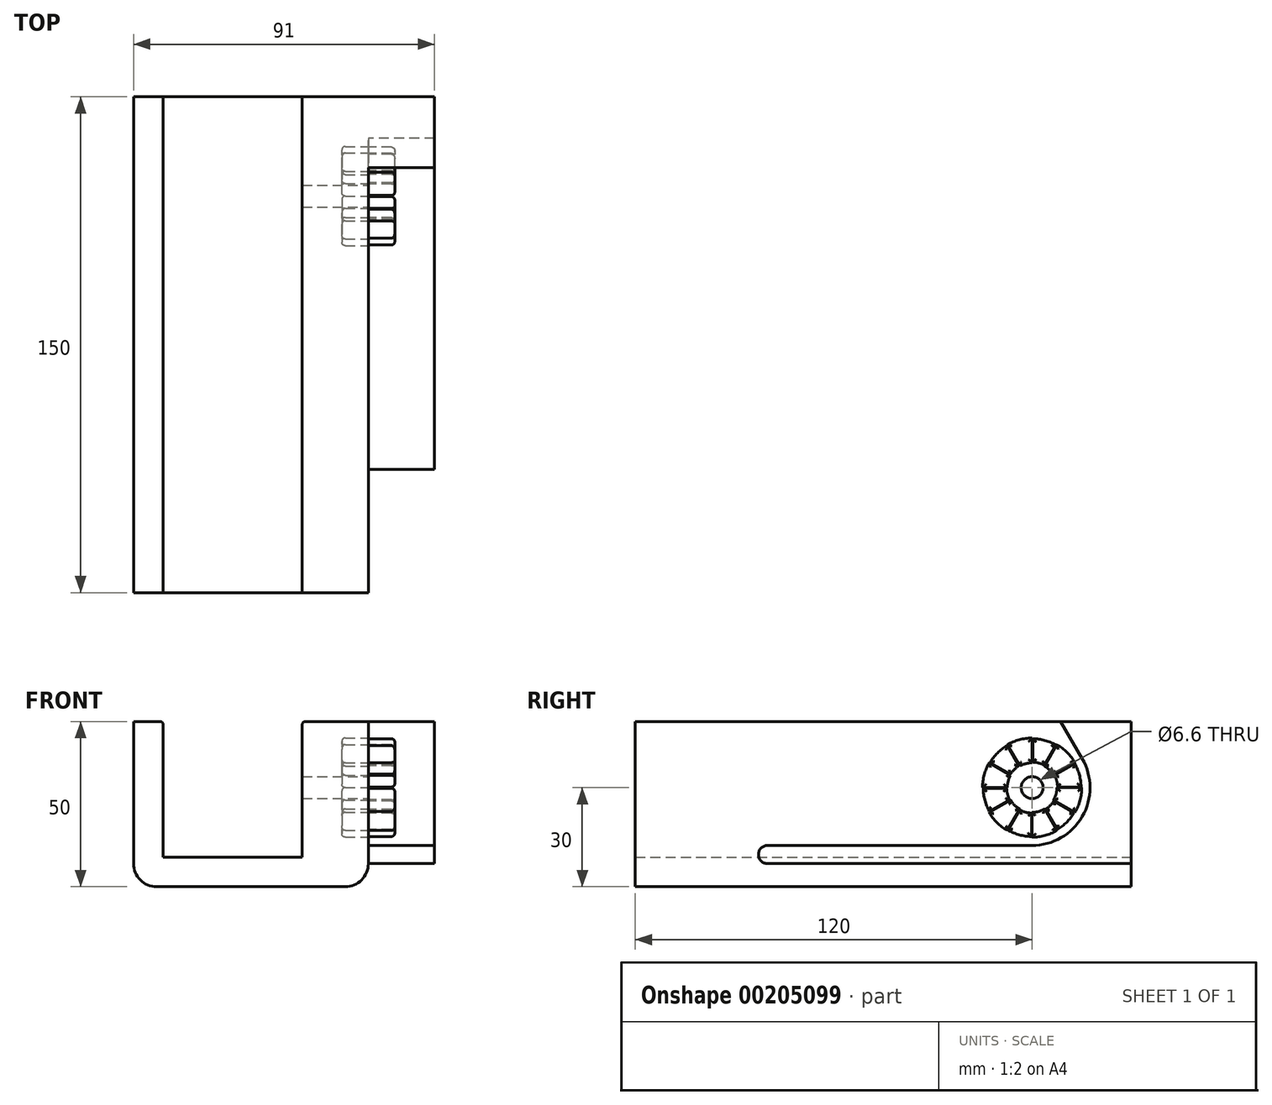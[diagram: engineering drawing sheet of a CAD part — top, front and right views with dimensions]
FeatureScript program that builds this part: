
annotation { "Feature Type Name" : "Feature", "Feature Type Description" : "" }
export const myFeature = defineFeature(function(context is Context, id is Id, definition is map)
    precondition{}
    {
        {
            var Q0;
            Q0=qCreatedBy(makeId("Front.planeOp"),FACE);
            var sketch = newSketch(context, id + "F7", { "sketchPlane" : qUnion([Q0])});
            skLineSegment(sketch, "E0", {"start": v(21, 0) * mm, "end": v(21, 40) * mm});
            skLineSegment(sketch, "E1", {"start": v(21, 0) * mm, "end": v(-21, 0) * mm});
            skLineSegment(sketch, "E2", {"start": v(-21, 0) * mm, "end": v(-21, 40) * mm});
            skLineSegment(sketch, "E3", {"start": v(-22, 41) * mm, "end": v(-30, 41) * mm});
            skLineSegment(sketch, "E4", {"start": v(-30, 41) * mm, "end": v(-30, -2) * mm});
            skLineSegment(sketch, "E5", {"start": v(-23, -9) * mm, "end": v(34, -9) * mm});
            skLineSegment(sketch, "E6", {"start": v(41, -2) * mm, "end": v(41, 41) * mm});
            skLineSegment(sketch, "E7", {"start": v(41, 41) * mm, "end": v(22, 41) * mm});
            skArc(sketch, "E8", {"start": v(22, 41) * mm, "mid": v(21.3, 40.7) * mm, "end": v(21, 40) * mm});
            skArc(sketch, "E9", {"start": v(-22, 41) * mm, "mid": v(-21.3, 40.7) * mm, "end": v(-21, 40) * mm});
            skPoint(sketch, "E10.visualSharp", {"position": v(41, -9) * mm});
            skArc(sketch, "E10.filletArc", {"start": v(34, -9) * mm, "mid": v(38.95, -6.95) * mm, "end": v(41, -2) * mm});
            skPoint(sketch, "E11.visualSharp", {"position": v(-30, -9) * mm});
            skArc(sketch, "E11.filletArc", {"start": v(-30, -2) * mm, "mid": v(-27.95, -6.95) * mm, "end": v(-23, -9) * mm});
            skPoint(sketch, "E12", {"position": v(0, 0) * mm});
            skPoint(sketch, "E13", {"position": v(-30, 19.5) * mm});
            skSolve(sketch);
        }
        {
            var Q0;
            Q0=makeQuery(id+"F7.imprint","IMPRINT",FACE,{"disambiguationData":[TD([[makeQuery(id+"F7.imprint","IMPRINT",EDGE,{"derivedFrom":sQuery(id+"F7.wireOp",EDGE,"E0")}),-1.0]])]});
            extrude(context, id + "F0", {"entities" : qUnion([Q0]), "depth" : 150 * mm});
        }
        {
            var Q0;
            Q0=makeQuery(id+"F0.opExtrude","SWEPT_FACE",FACE,{"disambiguationData":[OSD([sQuery(id+"F7.wireOp",EDGE,"E6")])]});
            var sketch = newSketch(context, id + "F1", { "sketchPlane" : qUnion([Q0])});
            skCircle(sketch, "E14", {"center": v(-30, 21) * mm, "radius": 3.3 * mm});
            skLineSegment(sketch, "E15", {"start": v(0, 41) * mm, "end": v(0, -2) * mm, "construction": true});
            skCircle(sketch, "E16", {"center": v(-30, 21) * mm, "radius": 17.5 * mm});
            skLineSegment(sketch, "E17", {"start": v(-21.34, 41) * mm, "end": v(-14.84, 29.75) * mm});
            skLineSegment(sketch, "E18", {"start": v(-30, 3.5) * mm, "end": v(-110, 3.5) * mm});
            skArc(sketch, "E19", {"start": v(-110, 3.5) * mm, "mid": v(-112.75, 0.75) * mm, "end": v(-110, -2) * mm});
            skLineSegment(sketch, "E20", {"start": v(-30, 28.5) * mm, "end": v(-30, 36) * mm});
            skLineSegment(sketch, "E21", {"start": v(-26.25, 27.5) * mm, "end": v(-26.25, 27.5) * mm});
            skLineSegment(sketch, "E22.anchor1", {"start": v(-30, 21) * mm, "end": v(-30, 28.5) * mm, "construction": true});
            skArc(sketch, "E23", {"start": v(-30, 36) * mm, "mid": v(-33.88, 6.51) * mm, "end": v(-22.5, 34) * mm});
            skArc(sketch, "E24", {"start": v(-22.5, 34) * mm, "mid": v(-26.12, 35.49) * mm, "end": v(-30, 36) * mm});
            skLineSegment(sketch, "E25", {"start": v(-26.25, 27.5) * mm, "end": v(-22.5, 34) * mm});
            skLineSegment(sketch, "E26", {"start": v(-30, 28.5) * mm, "end": v(-30, 28.5) * mm});
            skArc(sketch, "E27", {"start": v(-30, 28.5) * mm, "mid": v(-31.94, 13.76) * mm, "end": v(-26.25, 27.5) * mm});
            skArc(sketch, "E28", {"start": v(-26.25, 27.5) * mm, "mid": v(-28.06, 28.24) * mm, "end": v(-30, 28.5) * mm});
            skArc(sketch, "E29.0", {"start": v(-22.77, 33.92) * mm, "mid": v(-26.17, 35.3) * mm, "end": v(-29.8, 35.8) * mm});
            skLineSegment(sketch, "E29.1", {"start": v(-26.32, 27.77) * mm, "end": v(-22.77, 33.92) * mm});
            skArc(sketch, "E29.2", {"start": v(-26.32, 27.77) * mm, "mid": v(-28, 28.44) * mm, "end": v(-29.8, 28.7) * mm});
            skLineSegment(sketch, "E29.3", {"start": v(-29.8, 28.7) * mm, "end": v(-29.8, 35.8) * mm});
            skLineSegment(sketch, "E30.1.0", {"start": v(-36.57, 25.02) * mm, "end": v(-42.72, 28.57) * mm});
            skArc(sketch, "E30.1.1", {"start": v(-37.57, 33.72) * mm, "mid": v(-40.47, 31.47) * mm, "end": v(-42.72, 28.57) * mm});
            skLineSegment(sketch, "E30.1.2", {"start": v(-34.02, 27.57) * mm, "end": v(-37.57, 33.72) * mm});
            skArc(sketch, "E30.1.3", {"start": v(-34.02, 27.57) * mm, "mid": v(-35.44, 26.44) * mm, "end": v(-36.57, 25.02) * mm});
            skLineSegment(sketch, "E30.1.4", {"start": v(-33.75, 27.5) * mm, "end": v(-37.5, 34) * mm});
            skLineSegment(sketch, "E30.1.5", {"start": v(-36.5, 24.75) * mm, "end": v(-43, 28.5) * mm});
            skLineSegment(sketch, "E30.2.0", {"start": v(-36.77, 17.32) * mm, "end": v(-42.92, 13.77) * mm});
            skArc(sketch, "E30.2.1", {"start": v(-44.8, 20.8) * mm, "mid": v(-44.3, 17.17) * mm, "end": v(-42.92, 13.77) * mm});
            skLineSegment(sketch, "E30.2.2", {"start": v(-37.7, 20.8) * mm, "end": v(-44.8, 20.8) * mm});
            skArc(sketch, "E30.2.3", {"start": v(-37.7, 20.8) * mm, "mid": v(-37.44, 19) * mm, "end": v(-36.77, 17.32) * mm});
            skLineSegment(sketch, "E30.2.4", {"start": v(-37.5, 21) * mm, "end": v(-45, 21) * mm});
            skLineSegment(sketch, "E30.2.5", {"start": v(-36.5, 17.25) * mm, "end": v(-43, 13.5) * mm});
            skLineSegment(sketch, "E30.3.0", {"start": v(-30.2, 13.3) * mm, "end": v(-30.2, 6.2) * mm});
            skArc(sketch, "E30.3.1", {"start": v(-37.23, 8.08) * mm, "mid": v(-33.83, 6.7) * mm, "end": v(-30.2, 6.2) * mm});
            skLineSegment(sketch, "E30.3.2", {"start": v(-33.68, 14.23) * mm, "end": v(-37.23, 8.08) * mm});
            skArc(sketch, "E30.3.3", {"start": v(-33.68, 14.23) * mm, "mid": v(-32, 13.56) * mm, "end": v(-30.2, 13.3) * mm});
            skLineSegment(sketch, "E30.3.4", {"start": v(-33.75, 14.5) * mm, "end": v(-37.5, 8) * mm});
            skLineSegment(sketch, "E30.3.5", {"start": v(-30, 13.5) * mm, "end": v(-30, 6) * mm});
            skLineSegment(sketch, "E30.4.0", {"start": v(-23.43, 16.98) * mm, "end": v(-17.28, 13.43) * mm});
            skArc(sketch, "E30.4.1", {"start": v(-22.43, 8.28) * mm, "mid": v(-19.53, 10.53) * mm, "end": v(-17.28, 13.43) * mm});
            skLineSegment(sketch, "E30.4.2", {"start": v(-25.98, 14.43) * mm, "end": v(-22.43, 8.28) * mm});
            skArc(sketch, "E30.4.3", {"start": v(-25.98, 14.43) * mm, "mid": v(-24.56, 15.56) * mm, "end": v(-23.43, 16.98) * mm});
            skLineSegment(sketch, "E30.4.4", {"start": v(-26.25, 14.5) * mm, "end": v(-22.5, 8) * mm});
            skLineSegment(sketch, "E30.4.5", {"start": v(-23.5, 17.25) * mm, "end": v(-17, 13.5) * mm});
            skLineSegment(sketch, "E30.5.0", {"start": v(-23.23, 24.68) * mm, "end": v(-17.08, 28.23) * mm});
            skArc(sketch, "E30.5.1", {"start": v(-15.2, 21.2) * mm, "mid": v(-15.7, 24.83) * mm, "end": v(-17.08, 28.23) * mm});
            skLineSegment(sketch, "E30.5.2", {"start": v(-22.3, 21.2) * mm, "end": v(-15.2, 21.2) * mm});
            skArc(sketch, "E30.5.3", {"start": v(-22.3, 21.2) * mm, "mid": v(-22.56, 23) * mm, "end": v(-23.23, 24.68) * mm});
            skLineSegment(sketch, "E30.5.4", {"start": v(-22.5, 21) * mm, "end": v(-15, 21) * mm});
            skLineSegment(sketch, "E30.5.5", {"start": v(-23.5, 24.75) * mm, "end": v(-17, 28.5) * mm});
            skSolve(sketch);
        }
        {
            var Q0;
            {var subQ4=sQuery(id+"F1.wireOp",EDGE,"E17");Q0=makeQuery(id+"F1.imprint","IMPRINT",FACE,{"disambiguationData":[TD([[makeQuery(id+"F1.imprint","IMPRINT",EDGE,{"derivedFrom":subQ4}),1.0]])]});}
            extrude(context, id + "F2", {"entities" : qUnion([Q0]), "operationType" : NewBodyOperationType.ADD, "depth" : 20 * mm});
        }
        {
            var Q0;
            Q0=sQuery(id+"F1.wireOp",VERTEX,"E16.center");
            var Q1;
            Q1=makeQuery(id+"F0.opExtrude","SWEPT_BODY",BODY,{"disambiguationData":[OSD([sQuery(id+"F7.wireOp",EDGE,"E0"),sQuery(id+"F7.wireOp",EDGE,"E1"),sQuery(id+"F7.wireOp",EDGE,"E2"),sQuery(id+"F7.wireOp",EDGE,"E3"),sQuery(id+"F7.wireOp",EDGE,"E4"),sQuery(id+"F7.wireOp",EDGE,"E5"),sQuery(id+"F7.wireOp",EDGE,"E6"),sQuery(id+"F7.wireOp",EDGE,"E7"),sQuery(id+"F7.wireOp",EDGE,"E8"),sQuery(id+"F7.wireOp",EDGE,"E9"),sQuery(id+"F7.wireOp",EDGE,"E10.filletArc"),sQuery(id+"F7.wireOp",EDGE,"E11.filletArc")])]});
            hole(context, id + "F3", {"style" : HoleStyle.SIMPLE, "endStyle" : HoleEndStyle.BLIND, "standardTappedOrClearance" : lookupTablePath({ "standard" : "ISO", "fit" : "Normal", "size" : "M6", "type" : "Clearance" }), "standardBlindInLast" : lookupTablePath({ "fit" : "Standard", "standard" : "ISO", "size" : "M6", "type" : "Clearance" }), "holeDiameter" : 6.6 * mm, "holeDepth" : 25 * mm, "locations" : qUnion([Q0]), "scope" : qUnion([Q1])});
        }
        {
            var Q0;
            Q0=makeQuery(id+"F1.imprint","IMPRINT",FACE,{"disambiguationData":[TD([[makeQuery(id+"F1.imprint","IMPRINT",EDGE,{"derivedFrom":sQuery(id+"F1.wireOp",EDGE,"E29.0")}),1.0]])]});
            var Q1;
            Q1=makeQuery(id+"F1.imprint","IMPRINT",FACE,{"disambiguationData":[TD([[makeQuery(id+"F1.imprint","IMPRINT",EDGE,{"derivedFrom":sQuery(id+"F1.wireOp",EDGE,"E30.5.0")}),-1.0]])]});
            var Q2;
            Q2=makeQuery(id+"F1.imprint","IMPRINT",FACE,{"disambiguationData":[TD([[makeQuery(id+"F1.imprint","IMPRINT",EDGE,{"derivedFrom":sQuery(id+"F1.wireOp",EDGE,"E30.4.0")}),-1.0]])]});
            var Q3;
            Q3=makeQuery(id+"F1.imprint","IMPRINT",FACE,{"disambiguationData":[TD([[makeQuery(id+"F1.imprint","IMPRINT",EDGE,{"derivedFrom":sQuery(id+"F1.wireOp",EDGE,"E30.3.0")}),-1.0]])]});
            var Q4;
            Q4=makeQuery(id+"F1.imprint","IMPRINT",FACE,{"disambiguationData":[TD([[makeQuery(id+"F1.imprint","IMPRINT",EDGE,{"derivedFrom":sQuery(id+"F1.wireOp",EDGE,"E30.2.0")}),-1.0]])]});
            var Q5;
            Q5=makeQuery(id+"F1.imprint","IMPRINT",FACE,{"disambiguationData":[TD([[makeQuery(id+"F1.imprint","IMPRINT",EDGE,{"derivedFrom":sQuery(id+"F1.wireOp",EDGE,"E30.1.0")}),-1.0]])]});
            extrude(context, id + "F4", {"entities" : qUnion([Q0, Q1, Q2, Q3, Q4, Q5]), "operationType" : NewBodyOperationType.ADD, "depth" : 8 * mm});
        }
        {
            var Q0;
            {var subQ0=sQuery(id+"F1.wireOp",EDGE,"E20");Q0=makeQuery(id+"F1.imprint","IMPRINT",FACE,{"disambiguationData":[TD([[makeQuery(id+"F1.imprint","IMPRINT",EDGE,{"derivedFrom":subQ0}),1.0]])]});}
            var Q1;
            {var subQ0=sQuery(id+"F1.wireOp",EDGE,"E25");Q1=makeQuery(id+"F1.imprint","IMPRINT",FACE,{"disambiguationData":[TD([[makeQuery(id+"F1.imprint","IMPRINT",EDGE,{"derivedFrom":subQ0}),-1.0]])]});}
            var Q2;
            {var subQ0=sQuery(id+"F1.wireOp",EDGE,"E30.4.5");Q2=makeQuery(id+"F1.imprint","IMPRINT",FACE,{"disambiguationData":[TD([[makeQuery(id+"F1.imprint","IMPRINT",EDGE,{"derivedFrom":subQ0}),1.0]])]});}
            var Q3;
            {var subQ0=sQuery(id+"F1.wireOp",EDGE,"E30.3.5");Q3=makeQuery(id+"F1.imprint","IMPRINT",FACE,{"disambiguationData":[TD([[makeQuery(id+"F1.imprint","IMPRINT",EDGE,{"derivedFrom":subQ0}),1.0]])]});}
            var Q4;
            {var subQ0=sQuery(id+"F1.wireOp",EDGE,"E30.2.5");Q4=makeQuery(id+"F1.imprint","IMPRINT",FACE,{"disambiguationData":[TD([[makeQuery(id+"F1.imprint","IMPRINT",EDGE,{"derivedFrom":subQ0}),1.0]])]});}
            var Q5;
            {var subQ0=sQuery(id+"F1.wireOp",EDGE,"E30.1.5");Q5=makeQuery(id+"F1.imprint","IMPRINT",FACE,{"disambiguationData":[TD([[makeQuery(id+"F1.imprint","IMPRINT",EDGE,{"derivedFrom":subQ0}),1.0]])]});}
            extrude(context, id + "F5", {"entities" : qUnion([Q0, Q1, Q2, Q3, Q4, Q5]), "operationType" : NewBodyOperationType.REMOVE, "oppositeDirection" : true, "depth" : 8 * mm});
        }
        {
            var Q0;
            Q0=makeQuery(id+"F5.boolean.opBoolean","COPY",FACE,{"derivedFrom":makeQuery(id+"F5.opExtrude","CAP_FACE",FACE,{"disambiguationData":[OSD([sQuery(id+"F1.wireOp",EDGE,"E20"),sQuery(id+"F1.wireOp",EDGE,"E23"),sQuery(id+"F1.wireOp",EDGE,"E27"),sQuery(id+"F1.wireOp",EDGE,"E30.1.4")])],"isStart":false})});
            var Q1;
            Q1=makeQuery(id+"F5.boolean.opBoolean","COPY",FACE,{"derivedFrom":makeQuery(id+"F5.opExtrude","CAP_FACE",FACE,{"disambiguationData":[OSD([sQuery(id+"F1.wireOp",EDGE,"E23"),sQuery(id+"F1.wireOp",EDGE,"E25"),sQuery(id+"F1.wireOp",EDGE,"E27"),sQuery(id+"F1.wireOp",EDGE,"E30.5.5")])],"isStart":false})});
            var Q2;
            Q2=makeQuery(id+"F5.boolean.opBoolean","COPY",FACE,{"derivedFrom":makeQuery(id+"F5.opExtrude","CAP_FACE",FACE,{"disambiguationData":[OSD([sQuery(id+"F1.wireOp",EDGE,"E23"),sQuery(id+"F1.wireOp",EDGE,"E27"),sQuery(id+"F1.wireOp",EDGE,"E30.4.5"),sQuery(id+"F1.wireOp",EDGE,"E30.5.4")])],"isStart":false})});
            var Q3;
            Q3=makeQuery(id+"F5.boolean.opBoolean","COPY",FACE,{"derivedFrom":makeQuery(id+"F5.opExtrude","CAP_FACE",FACE,{"disambiguationData":[OSD([sQuery(id+"F1.wireOp",EDGE,"E23"),sQuery(id+"F1.wireOp",EDGE,"E27"),sQuery(id+"F1.wireOp",EDGE,"E30.3.5"),sQuery(id+"F1.wireOp",EDGE,"E30.4.4")])],"isStart":false})});
            var Q4;
            Q4=makeQuery(id+"F5.boolean.opBoolean","COPY",FACE,{"derivedFrom":makeQuery(id+"F5.opExtrude","CAP_FACE",FACE,{"disambiguationData":[OSD([sQuery(id+"F1.wireOp",EDGE,"E23"),sQuery(id+"F1.wireOp",EDGE,"E27"),sQuery(id+"F1.wireOp",EDGE,"E30.2.5"),sQuery(id+"F1.wireOp",EDGE,"E30.3.4")])],"isStart":false})});
            var Q5;
            Q5=makeQuery(id+"F5.boolean.opBoolean","COPY",FACE,{"derivedFrom":makeQuery(id+"F5.opExtrude","CAP_FACE",FACE,{"disambiguationData":[OSD([sQuery(id+"F1.wireOp",EDGE,"E23"),sQuery(id+"F1.wireOp",EDGE,"E27"),sQuery(id+"F1.wireOp",EDGE,"E30.1.5"),sQuery(id+"F1.wireOp",EDGE,"E30.2.4")])],"isStart":false})});
            var Q6;
            Q6=makeQuery(id+"F4.opExtrude","CAP_FACE",FACE,{"disambiguationData":[OSD([sQuery(id+"F1.wireOp",EDGE,"E30.1.0"),sQuery(id+"F1.wireOp",EDGE,"E30.1.1"),sQuery(id+"F1.wireOp",EDGE,"E30.1.2"),sQuery(id+"F1.wireOp",EDGE,"E30.1.3")])],"isStart":false});
            var Q7;
            Q7=makeQuery(id+"F4.opExtrude","CAP_FACE",FACE,{"disambiguationData":[OSD([sQuery(id+"F1.wireOp",EDGE,"E29.0"),sQuery(id+"F1.wireOp",EDGE,"E29.1"),sQuery(id+"F1.wireOp",EDGE,"E29.2"),sQuery(id+"F1.wireOp",EDGE,"E29.3")])],"isStart":false});
            var Q8;
            Q8=makeQuery(id+"F4.opExtrude","CAP_FACE",FACE,{"disambiguationData":[OSD([sQuery(id+"F1.wireOp",EDGE,"E30.5.0"),sQuery(id+"F1.wireOp",EDGE,"E30.5.1"),sQuery(id+"F1.wireOp",EDGE,"E30.5.2"),sQuery(id+"F1.wireOp",EDGE,"E30.5.3")])],"isStart":false});
            var Q9;
            Q9=makeQuery(id+"F4.opExtrude","CAP_FACE",FACE,{"disambiguationData":[OSD([sQuery(id+"F1.wireOp",EDGE,"E30.4.0"),sQuery(id+"F1.wireOp",EDGE,"E30.4.1"),sQuery(id+"F1.wireOp",EDGE,"E30.4.2"),sQuery(id+"F1.wireOp",EDGE,"E30.4.3")])],"isStart":false});
            var Q10;
            Q10=makeQuery(id+"F4.opExtrude","CAP_FACE",FACE,{"disambiguationData":[OSD([sQuery(id+"F1.wireOp",EDGE,"E30.3.0"),sQuery(id+"F1.wireOp",EDGE,"E30.3.1"),sQuery(id+"F1.wireOp",EDGE,"E30.3.2"),sQuery(id+"F1.wireOp",EDGE,"E30.3.3")])],"isStart":false});
            var Q11;
            Q11=makeQuery(id+"F4.opExtrude","CAP_FACE",FACE,{"disambiguationData":[OSD([sQuery(id+"F1.wireOp",EDGE,"E30.2.0"),sQuery(id+"F1.wireOp",EDGE,"E30.2.1"),sQuery(id+"F1.wireOp",EDGE,"E30.2.2"),sQuery(id+"F1.wireOp",EDGE,"E30.2.3")])],"isStart":false});
            var Q12;
            {var subQ0=sQuery(id+"F1.wireOp",EDGE,"E27");Q12=makeQuery(id+"F5.boolean.opBoolean","COPY",EDGE,{"derivedFrom":makeQuery(id+"F5.opExtrude","CAP_EDGE",EDGE,{"disambiguationData":[OSD([subQ0]),TDD([makeQuery(id+"F1.imprint","IMPRINT",EDGE,{"disambiguationData":[TD([[makeQuery(id+"F1.imprint","INTERSECT",VERTEX,{"derivedFrom":[subQ0,sQuery(id+"F1.wireOp",EDGE,"E30.1.5")]}),-1.0]])],"derivedFrom":subQ0})])],"isStart":true})});}
            var Q13;
            {var subQ0=sQuery(id+"F1.wireOp",EDGE,"E27");Q13=makeQuery(id+"F5.boolean.opBoolean","COPY",EDGE,{"derivedFrom":makeQuery(id+"F5.opExtrude","CAP_EDGE",EDGE,{"disambiguationData":[OSD([subQ0]),TDD([makeQuery(id+"F1.imprint","IMPRINT",EDGE,{"disambiguationData":[TD([[makeQuery(id+"F1.imprint","INTERSECT",VERTEX,{"derivedFrom":[subQ0,sQuery(id+"F1.wireOp",EDGE,"E30.1.4")]}),1.0]])],"derivedFrom":subQ0})])],"isStart":true})});}
            var Q14;
            {var subQ0=sQuery(id+"F1.wireOp",EDGE,"E27");Q14=makeQuery(id+"F5.boolean.opBoolean","COPY",EDGE,{"derivedFrom":makeQuery(id+"F5.opExtrude","CAP_EDGE",EDGE,{"disambiguationData":[OSD([subQ0]),TDD([makeQuery(id+"F1.imprint","IMPRINT",EDGE,{"disambiguationData":[TD([[makeQuery(id+"F1.imprint","INTERSECT",VERTEX,{"derivedFrom":[subQ0,sQuery(id+"F1.wireOp",EDGE,"E30.5.5")]}),-1.0]])],"derivedFrom":subQ0})])],"isStart":true})});}
            var Q15;
            {var subQ0=sQuery(id+"F1.wireOp",EDGE,"E27");Q15=makeQuery(id+"F5.boolean.opBoolean","COPY",EDGE,{"derivedFrom":makeQuery(id+"F5.opExtrude","CAP_EDGE",EDGE,{"disambiguationData":[OSD([subQ0]),TDD([makeQuery(id+"F1.imprint","IMPRINT",EDGE,{"disambiguationData":[TD([[makeQuery(id+"F1.imprint","INTERSECT",VERTEX,{"derivedFrom":[subQ0,sQuery(id+"F1.wireOp",EDGE,"E30.4.5")]}),-1.0]])],"derivedFrom":subQ0})])],"isStart":true})});}
            var Q16;
            {var subQ0=sQuery(id+"F1.wireOp",EDGE,"E27");Q16=makeQuery(id+"F5.boolean.opBoolean","COPY",EDGE,{"derivedFrom":makeQuery(id+"F5.opExtrude","CAP_EDGE",EDGE,{"disambiguationData":[OSD([subQ0]),TDD([makeQuery(id+"F1.imprint","IMPRINT",EDGE,{"disambiguationData":[TD([[makeQuery(id+"F1.imprint","INTERSECT",VERTEX,{"derivedFrom":[subQ0,sQuery(id+"F1.wireOp",EDGE,"E30.3.5")]}),-1.0]])],"derivedFrom":subQ0})])],"isStart":true})});}
            var Q17;
            {var subQ0=sQuery(id+"F1.wireOp",EDGE,"E27");Q17=makeQuery(id+"F5.boolean.opBoolean","COPY",EDGE,{"derivedFrom":makeQuery(id+"F5.opExtrude","CAP_EDGE",EDGE,{"disambiguationData":[OSD([subQ0]),TDD([makeQuery(id+"F1.imprint","IMPRINT",EDGE,{"disambiguationData":[TD([[makeQuery(id+"F1.imprint","INTERSECT",VERTEX,{"derivedFrom":[subQ0,sQuery(id+"F1.wireOp",EDGE,"E30.2.5")]}),-1.0]])],"derivedFrom":subQ0})])],"isStart":true})});}
            var Q18;
            {var subQ0=sQuery(id+"F1.wireOp",EDGE,"E23");Q18=makeQuery(id+"F5.boolean.opBoolean","COPY",EDGE,{"derivedFrom":makeQuery(id+"F5.opExtrude","CAP_EDGE",EDGE,{"disambiguationData":[OSD([subQ0]),TDD([makeQuery(id+"F1.imprint","IMPRINT",EDGE,{"disambiguationData":[TD([[makeQuery(id+"F1.imprint","INTERSECT",VERTEX,{"derivedFrom":[subQ0,sQuery(id+"F1.wireOp",EDGE,"E30.1.5")]}),-1.0]])],"derivedFrom":subQ0})])],"isStart":true})});}
            var Q19;
            {var subQ0=sQuery(id+"F1.wireOp",EDGE,"E23");Q19=makeQuery(id+"F5.boolean.opBoolean","COPY",EDGE,{"derivedFrom":makeQuery(id+"F5.opExtrude","CAP_EDGE",EDGE,{"disambiguationData":[OSD([subQ0]),TDD([makeQuery(id+"F1.imprint","IMPRINT",EDGE,{"disambiguationData":[TD([[makeQuery(id+"F1.imprint","INTERSECT",VERTEX,{"derivedFrom":[subQ0,sQuery(id+"F1.wireOp",EDGE,"E30.1.4")]}),1.0]])],"derivedFrom":subQ0})])],"isStart":true})});}
            var Q20;
            {var subQ0=sQuery(id+"F1.wireOp",EDGE,"E23");Q20=makeQuery(id+"F5.boolean.opBoolean","COPY",EDGE,{"derivedFrom":makeQuery(id+"F5.opExtrude","CAP_EDGE",EDGE,{"disambiguationData":[OSD([subQ0]),TDD([makeQuery(id+"F1.imprint","IMPRINT",EDGE,{"disambiguationData":[TD([[makeQuery(id+"F1.imprint","INTERSECT",VERTEX,{"derivedFrom":[subQ0,sQuery(id+"F1.wireOp",EDGE,"E30.5.5")]}),-1.0]])],"derivedFrom":subQ0})])],"isStart":true})});}
            var Q21;
            {var subQ0=sQuery(id+"F1.wireOp",EDGE,"E23");Q21=makeQuery(id+"F5.boolean.opBoolean","COPY",EDGE,{"derivedFrom":makeQuery(id+"F5.opExtrude","CAP_EDGE",EDGE,{"disambiguationData":[OSD([subQ0]),TDD([makeQuery(id+"F1.imprint","IMPRINT",EDGE,{"disambiguationData":[TD([[makeQuery(id+"F1.imprint","INTERSECT",VERTEX,{"derivedFrom":[subQ0,sQuery(id+"F1.wireOp",EDGE,"E30.4.5")]}),-1.0]])],"derivedFrom":subQ0})])],"isStart":true})});}
            var Q22;
            {var subQ0=sQuery(id+"F1.wireOp",EDGE,"E23");Q22=makeQuery(id+"F5.boolean.opBoolean","COPY",EDGE,{"derivedFrom":makeQuery(id+"F5.opExtrude","CAP_EDGE",EDGE,{"disambiguationData":[OSD([subQ0]),TDD([makeQuery(id+"F1.imprint","IMPRINT",EDGE,{"disambiguationData":[TD([[makeQuery(id+"F1.imprint","INTERSECT",VERTEX,{"derivedFrom":[subQ0,sQuery(id+"F1.wireOp",EDGE,"E30.3.5")]}),-1.0]])],"derivedFrom":subQ0})])],"isStart":true})});}
            var Q23;
            {var subQ0=sQuery(id+"F1.wireOp",EDGE,"E23");Q23=makeQuery(id+"F5.boolean.opBoolean","COPY",EDGE,{"derivedFrom":makeQuery(id+"F5.opExtrude","CAP_EDGE",EDGE,{"disambiguationData":[OSD([subQ0]),TDD([makeQuery(id+"F1.imprint","IMPRINT",EDGE,{"disambiguationData":[TD([[makeQuery(id+"F1.imprint","INTERSECT",VERTEX,{"derivedFrom":[subQ0,sQuery(id+"F1.wireOp",EDGE,"E30.2.5")]}),-1.0]])],"derivedFrom":subQ0})])],"isStart":true})});}
            fillet(context, id + "F6", {"entities" : qUnion([Q0, Q1, Q2, Q3, Q4, Q5, Q6, Q7, Q8, Q9, Q10, Q11, Q12, Q13, Q14, Q15, Q16, Q17, Q18, Q19, Q20, Q21, Q22, Q23]), "radius" : 1 * mm, "allowEdgeOverflow" : false});
        }
    });
